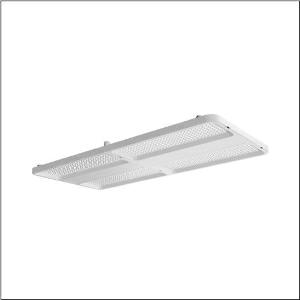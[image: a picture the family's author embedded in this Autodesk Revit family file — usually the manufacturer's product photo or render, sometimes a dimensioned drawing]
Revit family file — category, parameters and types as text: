
# Revit family: highbay_21_maxi_52hn11db4mda02
name_source: partatom
category: Lighting Fixtures
units: mm (PartAtom-declared; Revit-internal decimal feet)

## family parameters
Cut with Voids When Loaded = No
Host = Face
Light Source = No
Part Type = Normal
Room Calculation Point = No
Round Connector Dimension = Use Diameter
Shared = No

## types (1)
- --- (1 x LED, 28000 lm, 144.5 W, 4000K)
    Apparent Load = 144 VA
    CIE Flux Codes = 89 97 99 100 100
    Color Rendering = 80
    Color Temperature = 4000K
    Default Elevation = 1800 mm
    Description = high bay luminaire Highbay 21 maxi; direct symmetric narrow distribution, light control with lens of PMMA; UGR ≤ 19 (X = 4H | Y = 8H | S = 0.25H | reflection values 70/50/20); luminous flux: 28.000lm; light colour: 840, colour temperature: 4000K, MacAdam ≤ 3 SDCM (initial), colour rendering: CRI > 80; luminous efficacy: 193,8lm/W; rated service life: 75.000h (L80) at AT= ta max; control: Bluetooth Mesh; for wireless networking: Node luminaire for setting up a local control solution without a higher-level application controller, intelligence completely in the luminaire; no control line such as DALI between the Node multi-sensor luminaires and Nodes is required, wireless integration of other Node luminaires and Node multi-sensor luminaires into the network is possible; number of Node luminaires in the project can be expanded as required, network sizes > 300 Nodes can be realized; can also be connected to lighting or building automation via various gateways upon request; integrated DALI2 ECG provides luminaire data (according to IEC62386, Part 251), energy data (Part 252), and monitoring and analytics data (Part 253) to higher-level systems for further processing; luminaire connection: terminal, 5-pole, max. 2.5mm² (cable entry for one cable, Ø 8.5..16mm); mains connection: 230..240V, AC 50/60Hz; connected load: 144,5W; protection rating (complete): IP66; insulation class (complete): insulation class I (protective earthing); protection symbol: D; impact resistance: IK08; certification: CE, UKCA; internal wiring halogen-free; luminaire LABS conformity tested according to VDMA 24364:2018-05; Suitable for use in the food industry according to the specifications of IFS-Food, HACCP and/or BRC; housing frame of high-performance plastic PA6, matt traffic white (RAL 9016); cover of PMMA; dimension (LxWxH): 946 x 442 x 72mm; permissible operating ambient temperature: -20..+45°C (reducing of maximum allowable ambient temperature of 5°C with ceiling mounting); packaging unit: 1 piece; (delivery without accessories; please order mounting accessories separately)
    Height = 72 mm  [stored 0.23622 ft]
    Lamp = 1 x LED
    Lamp Light Flux = 28000 lm
    Lamp Power = 144.5 W
    Lamp count = 1
    Length = 946 mm
    Luminous efficacy = 194 lm/W
    Manufacturer = Siteco
    ModVariant = No
    Model = 52HN11DB4MDA02
    Mounting Place = Ceiling
    Mounting Type = Pendant
    Number of Poles = 1
    OnlyDefault = Yes
    Power Factor = 1
    Product Name = Highbay 21 maxi
    Product group = high bay luminaire
    ProductGroupID = 902
    Protection Class = Protection class I
    Protection Degree = IP 66
    RLX_Detail_Level = 1
    RLX_Emergency_Light_Flux = 0 lm
    RLX_Emergency_Type = 0
    RLX_Emergency_Type_DB = No
    RlxData = <blob elided: 128417 chars, md5=0afb069d>
    Socket = socket
    Standby Power = 0 W
    System Light Flux = 28000 lm
    System Power = 144 W
    Type Comments = factory setting: luminous flux: 100 % | dim-lin: 254 | 668 mA
    Type Image = l_1363244.jpg
    URL = http://relux.com
    VarID = @adj_012533
    Voltage = 0 V
    Weight = 0.00 kg
    Width = 442 mm

note: [stored X ft] marks values corroborated as IEEE doubles in the binary element streams (Revit-internal decimal feet)

## geometry (parser evidence)
native form markers: Blend x4, Sweep x9
no freeform markers — native parametric forms only
